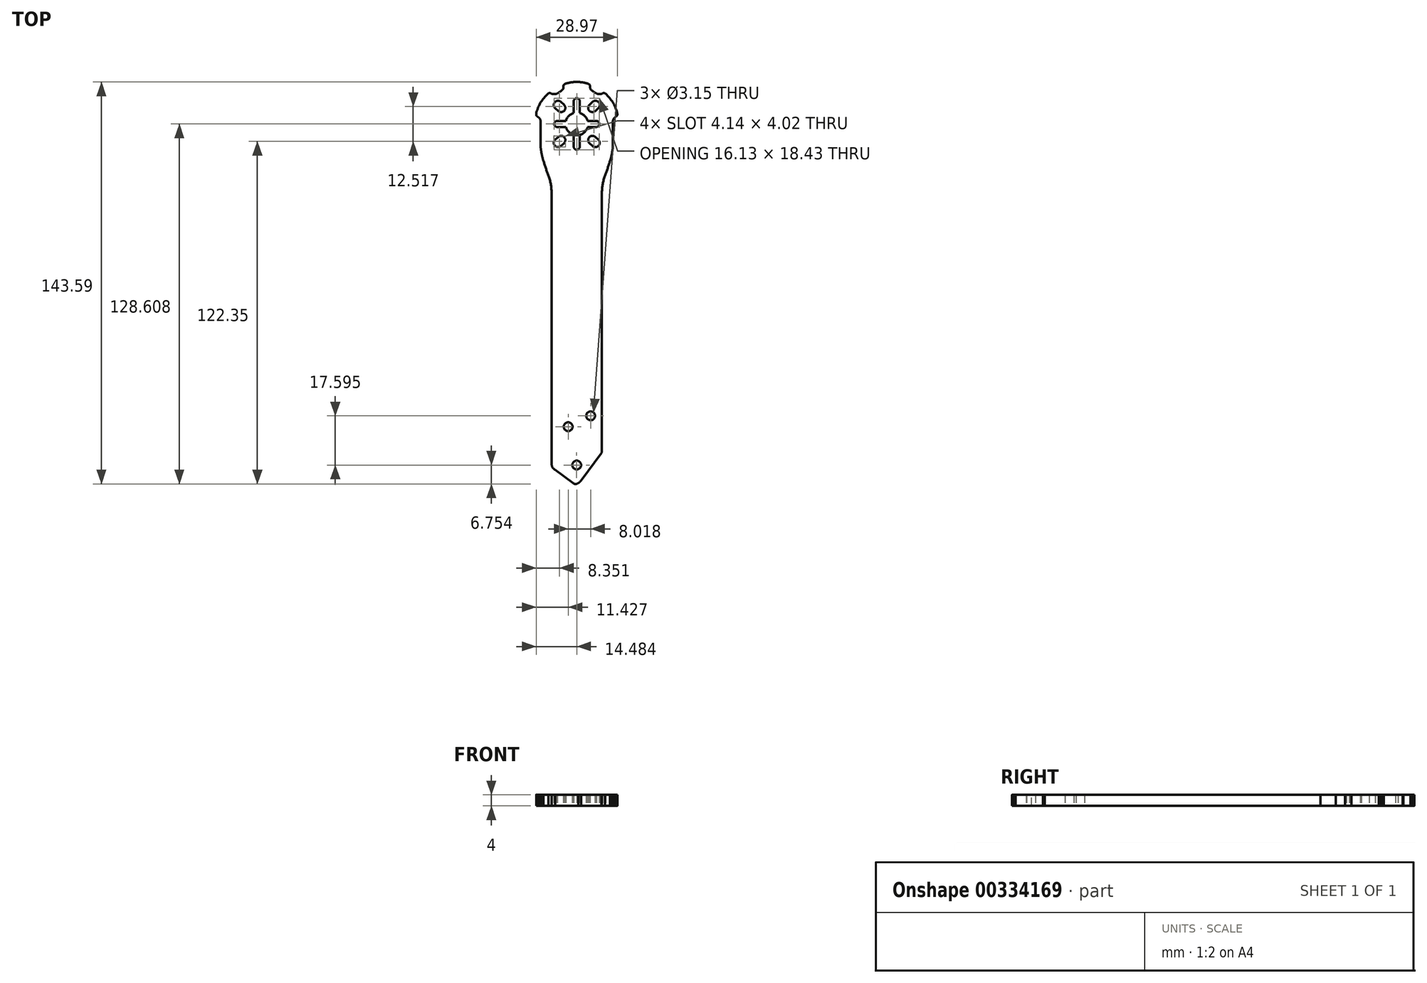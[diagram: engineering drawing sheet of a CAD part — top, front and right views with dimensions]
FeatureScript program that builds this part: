
annotation { "Feature Type Name" : "Feature", "Feature Type Description" : "" }
export const myFeature = defineFeature(function(context is Context, id is Id, definition is map)
    precondition{}
    {
        {
            var Q0;
            Q0=qCreatedBy(makeId("Top.planeOp"),FACE);
            var sketch = newSketch(context, id + "F0", { "sketchPlane" : qUnion([Q0])});
            skCircle(sketch, "E0", {"center": v(-4.22, -64.34) * mm, "radius": 1.57 * mm});
            skCircle(sketch, "E1", {"center": v(-12.24, -68.23) * mm, "radius": 1.57 * mm});
            skCircle(sketch, "E2", {"center": v(-9.2, -81.94) * mm, "radius": 1.57 * mm});
            skArc(sketch, "E3", {"start": v(-5.3, 41) * mm, "mid": v(-6.34, 42.79) * mm, "end": v(-8.13, 43.83) * mm});
            skArc(sketch, "E4", {"start": v(-1.12, 39.92) * mm, "mid": v(-1.4, 40.66) * mm, "end": v(-2.13, 41) * mm});
            skArc(sketch, "E5", {"start": v(-8.13, 48.05) * mm, "mid": v(-8.45, 48.82) * mm, "end": v(-9.22, 49.13) * mm});
            skLineSegment(sketch, "E6", {"start": v(-2.13, 41) * mm, "end": v(-5.3, 41) * mm});
            skLineSegment(sketch, "E7", {"start": v(-8.13, 48.05) * mm, "end": v(-8.13, 43.83) * mm});
            skLineSegment(sketch, "E8", {"start": v(-2.16, 45.18) * mm, "end": v(-2.16, 45.18) * mm});
            skArc(sketch, "E9", {"start": v(-4.61, 46.83) * mm, "mid": v(-4.74, 44.68) * mm, "end": v(-2.58, 44.55) * mm});
            skLineSegment(sketch, "E10", {"start": v(-3.52, 47.8) * mm, "end": v(-4.61, 46.83) * mm});
            skLineSegment(sketch, "E11", {"start": v(-2.58, 44.55) * mm, "end": v(-1.5, 45.52) * mm});
            skArc(sketch, "E12.trimOffspring", {"start": v(-1.5, 45.52) * mm, "mid": v(-1.37, 47.68) * mm, "end": v(-3.52, 47.8) * mm});
            skArc(sketch, "E13.MirrorCS", {"start": v(-1.5, 34.31) * mm, "mid": v(-1.37, 32.16) * mm, "end": v(-3.52, 32.03) * mm});
            skLineSegment(sketch, "E14.MirrorCS", {"start": v(-3.52, 32.03) * mm, "end": v(-4.61, 33) * mm});
            skArc(sketch, "E15.MirrorCS", {"start": v(-4.61, 33) * mm, "mid": v(-4.74, 35.16) * mm, "end": v(-2.58, 35.29) * mm});
            skLineSegment(sketch, "E16.MirrorCS", {"start": v(-2.58, 35.29) * mm, "end": v(-1.5, 34.31) * mm});
            skArc(sketch, "E17.MirrorCS", {"start": v(-1.12, 39.92) * mm, "mid": v(-1.4, 39.18) * mm, "end": v(-2.13, 38.84) * mm});
            skLineSegment(sketch, "E18.MirrorCS", {"start": v(-8.13, 31.79) * mm, "end": v(-8.13, 36) * mm});
            skLineSegment(sketch, "E19.MirrorCS", {"start": v(-2.13, 38.84) * mm, "end": v(-5.3, 38.84) * mm});
            skArc(sketch, "E20.MirrorCS", {"start": v(-5.3, 38.84) * mm, "mid": v(-6.34, 37.05) * mm, "end": v(-8.13, 36) * mm});
            skArc(sketch, "E21.MirrorCS", {"start": v(-8.13, 31.79) * mm, "mid": v(-8.45, 31.02) * mm, "end": v(-9.22, 30.7) * mm});
            skArc(sketch, "E22", {"start": v(0.93, 21.46) * mm, "mid": v(0.09, 18.5) * mm, "end": v(-0.19, 15.46) * mm});
            skArc(sketch, "E23", {"start": v(0.93, 21.46) * mm, "mid": v(1.86, 24.11) * mm, "end": v(2.71, 26.8) * mm});
            skArc(sketch, "E24", {"start": v(2.71, 26.8) * mm, "mid": v(3.17, 28.42) * mm, "end": v(3.5, 30.09) * mm});
            skArc(sketch, "E25", {"start": v(3.5, 30.09) * mm, "mid": v(3.66, 31.29) * mm, "end": v(3.74, 32.5) * mm});
            skLineSegment(sketch, "E26", {"start": v(3.74, 32.5) * mm, "end": v(3.74, 40.9) * mm});
            skArc(sketch, "E27", {"start": v(4.33, 42.17) * mm, "mid": v(3.9, 41.6) * mm, "end": v(3.74, 40.9) * mm});
            skArc(sketch, "E28", {"start": v(4.95, 42.62) * mm, "mid": v(4.64, 42.4) * mm, "end": v(4.33, 42.17) * mm});
            skArc(sketch, "E29", {"start": v(4.95, 42.62) * mm, "mid": v(5.2, 42.9) * mm, "end": v(5.3, 43.27) * mm});
            skArc(sketch, "E30", {"start": v(5.3, 43.27) * mm, "mid": v(5.28, 43.63) * mm, "end": v(5.2, 43.98) * mm});
            skArc(sketch, "E31", {"start": v(5.2, 43.98) * mm, "mid": v(3.66, 47.64) * mm, "end": v(1.1, 50.68) * mm});
            skArc(sketch, "E32", {"start": v(1.1, 50.68) * mm, "mid": v(0.6, 50.95) * mm, "end": v(0.04, 50.85) * mm});
            skArc(sketch, "E33", {"start": v(-2.22, 50.85) * mm, "mid": v(-1.09, 50.55) * mm, "end": v(0.04, 50.85) * mm});
            skArc(sketch, "E34", {"start": v(-4.01, 52.04) * mm, "mid": v(-3.15, 51.4) * mm, "end": v(-2.22, 50.85) * mm});
            skArc(sketch, "E35", {"start": v(-4.39, 52.76) * mm, "mid": v(-4.27, 52.36) * mm, "end": v(-4.01, 52.04) * mm});
            skArc(sketch, "E36", {"start": v(-4.45, 53.55) * mm, "mid": v(-4.42, 53.15) * mm, "end": v(-4.39, 52.76) * mm});
            skArc(sketch, "E37", {"start": v(-4.45, 53.55) * mm, "mid": v(-4.62, 53.95) * mm, "end": v(-4.96, 54.22) * mm});
            skArc(sketch, "E38", {"start": v(-4.96, 54.22) * mm, "mid": v(-7.06, 54.75) * mm, "end": v(-9.22, 54.9) * mm});
            skArc(sketch, "E39", {"start": v(-18.19, -81.72) * mm, "mid": v(-17.77, -82.83) * mm, "end": v(-16.92, -83.66) * mm});
            skLineSegment(sketch, "E40", {"start": v(-16.92, -83.66) * mm, "end": v(-10.54, -88.38) * mm});
            skArc(sketch, "E41", {"start": v(-10.54, -88.38) * mm, "mid": v(-9.6, -88.7) * mm, "end": v(-8.66, -88.38) * mm});
            skArc(sketch, "E42", {"start": v(-8.66, -88.38) * mm, "mid": v(-8.1, -87.97) * mm, "end": v(-7.64, -87.45) * mm});
            skLineSegment(sketch, "E43", {"start": v(-7.64, -87.45) * mm, "end": v(-0.42, -77.68) * mm});
            skArc(sketch, "E44", {"start": v(-0.42, -77.68) * mm, "mid": v(-0.26, -77.4) * mm, "end": v(-0.19, -77.07) * mm});
            skPoint(sketch, "E45", {"position": v(-9.19, 15.46) * mm});
            skLineSegment(sketch, "E46", {"start": v(-9.19, 54.9) * mm, "end": v(-9.19, -88.64) * mm});
            skArc(sketch, "E47.MirrorCS", {"start": v(-13.4, 54.22) * mm, "mid": v(-11.31, 54.75) * mm, "end": v(-9.15, 54.9) * mm});
            skArc(sketch, "E48.MirrorCS", {"start": v(-13.92, 53.55) * mm, "mid": v(-13.75, 53.95) * mm, "end": v(-13.4, 54.22) * mm});
            skArc(sketch, "E49.MirrorCS", {"start": v(-13.92, 53.55) * mm, "mid": v(-13.95, 53.15) * mm, "end": v(-13.98, 52.76) * mm});
            skArc(sketch, "E50.MirrorCS", {"start": v(-13.98, 52.76) * mm, "mid": v(-14.1, 52.36) * mm, "end": v(-14.36, 52.04) * mm});
            skArc(sketch, "E51.MirrorCS", {"start": v(-14.36, 52.04) * mm, "mid": v(-15.22, 51.4) * mm, "end": v(-16.16, 50.85) * mm});
            skArc(sketch, "E52.MirrorCS", {"start": v(-16.16, 50.85) * mm, "mid": v(-17.29, 50.55) * mm, "end": v(-18.42, 50.85) * mm});
            skArc(sketch, "E53.MirrorCS", {"start": v(-19.48, 50.68) * mm, "mid": v(-18.98, 50.95) * mm, "end": v(-18.42, 50.85) * mm});
            skArc(sketch, "E54.MirrorCS", {"start": v(-23.57, 43.98) * mm, "mid": v(-22.03, 47.64) * mm, "end": v(-19.48, 50.68) * mm});
            skArc(sketch, "E55.MirrorCS", {"start": v(-16.88, 45.52) * mm, "mid": v(-17, 47.68) * mm, "end": v(-14.85, 47.8) * mm});
            skLineSegment(sketch, "E56.MirrorCS", {"start": v(-14.85, 47.8) * mm, "end": v(-13.76, 46.83) * mm});
            skArc(sketch, "E57.MirrorCS", {"start": v(-13.76, 46.83) * mm, "mid": v(-13.63, 44.68) * mm, "end": v(-15.79, 44.55) * mm});
            skLineSegment(sketch, "E58.MirrorCS", {"start": v(-15.79, 44.55) * mm, "end": v(-16.88, 45.52) * mm});
            skArc(sketch, "E59.MirrorCS", {"start": v(-10.24, 48.05) * mm, "mid": v(-9.92, 48.82) * mm, "end": v(-9.15, 49.13) * mm});
            skLineSegment(sketch, "E60.MirrorCS", {"start": v(-10.24, 48.05) * mm, "end": v(-10.24, 43.83) * mm});
            skArc(sketch, "E61.MirrorCS", {"start": v(-23.67, 43.27) * mm, "mid": v(-23.65, 43.63) * mm, "end": v(-23.57, 43.98) * mm});
            skArc(sketch, "E62.MirrorCS", {"start": v(-23.32, 42.62) * mm, "mid": v(-23.57, 42.9) * mm, "end": v(-23.67, 43.27) * mm});
            skArc(sketch, "E63.MirrorCS", {"start": v(-23.32, 42.62) * mm, "mid": v(-23, 42.4) * mm, "end": v(-22.7, 42.17) * mm});
            skArc(sketch, "E64.MirrorCS", {"start": v(-22.7, 42.17) * mm, "mid": v(-22.27, 41.6) * mm, "end": v(-22.11, 40.9) * mm});
            skLineSegment(sketch, "E65.MirrorCS", {"start": v(-22.11, 32.5) * mm, "end": v(-22.11, 40.9) * mm});
            skArc(sketch, "E66.MirrorCS", {"start": v(-13.07, 41) * mm, "mid": v(-12.03, 42.79) * mm, "end": v(-10.24, 43.83) * mm});
            skLineSegment(sketch, "E67.MirrorCS", {"start": v(-16.25, 41) * mm, "end": v(-13.07, 41) * mm});
            skArc(sketch, "E68.MirrorCS", {"start": v(-17.25, 39.92) * mm, "mid": v(-16.96, 40.66) * mm, "end": v(-16.25, 41) * mm});
            skArc(sketch, "E69.MirrorCS", {"start": v(-17.25, 39.92) * mm, "mid": v(-16.96, 39.18) * mm, "end": v(-16.25, 38.84) * mm});
            skLineSegment(sketch, "E70.MirrorCS", {"start": v(-16.25, 38.84) * mm, "end": v(-13.07, 38.84) * mm});
            skArc(sketch, "E71.MirrorCS", {"start": v(-13.07, 38.84) * mm, "mid": v(-12.03, 37.05) * mm, "end": v(-10.24, 36) * mm});
            skLineSegment(sketch, "E72.MirrorCS", {"start": v(-10.24, 31.79) * mm, "end": v(-10.24, 36) * mm});
            skArc(sketch, "E73.MirrorCS", {"start": v(-10.24, 31.79) * mm, "mid": v(-9.92, 31.02) * mm, "end": v(-9.15, 30.7) * mm});
            skArc(sketch, "E74.MirrorCS", {"start": v(-13.76, 33) * mm, "mid": v(-13.63, 35.16) * mm, "end": v(-15.79, 35.29) * mm});
            skLineSegment(sketch, "E75.MirrorCS", {"start": v(-15.79, 35.29) * mm, "end": v(-16.88, 34.31) * mm});
            skArc(sketch, "E76.MirrorCS", {"start": v(-16.88, 34.31) * mm, "mid": v(-17, 32.16) * mm, "end": v(-14.85, 32.03) * mm});
            skLineSegment(sketch, "E77.MirrorCS", {"start": v(-14.85, 32.03) * mm, "end": v(-13.76, 33) * mm});
            skArc(sketch, "E78.MirrorCS", {"start": v(-21.87, 30.09) * mm, "mid": v(-22.04, 31.29) * mm, "end": v(-22.11, 32.5) * mm});
            skArc(sketch, "E79.MirrorCS", {"start": v(-21.08, 26.8) * mm, "mid": v(-21.55, 28.42) * mm, "end": v(-21.87, 30.09) * mm});
            skArc(sketch, "E80.MirrorCS", {"start": v(-19.3, 21.46) * mm, "mid": v(-20.23, 24.11) * mm, "end": v(-21.08, 26.8) * mm});
            skArc(sketch, "E81.MirrorCS", {"start": v(-19.3, 21.46) * mm, "mid": v(-18.46, 18.5) * mm, "end": v(-18.19, 15.46) * mm});
            skLineSegment(sketch, "E82", {"start": v(-12.24, -68.23) * mm, "end": v(-9.19, -68.23) * mm});
            skLineSegment(sketch, "E83", {"start": v(-4.22, -64.34) * mm, "end": v(-9.19, -64.34) * mm});
            skLineSegment(sketch, "E84.trimOffspring", {"start": v(-18.19, 15.46) * mm, "end": v(-18.19, 15.46) * mm});
            skLineSegment(sketch, "E85", {"start": v(-18.19, 15.46) * mm, "end": v(-18.19, -81.73) * mm});
            skLineSegment(sketch, "E86", {"start": v(-0.19, 15.46) * mm, "end": v(-0.19, -77.07) * mm});
            skLineSegment(sketch, "E87", {"start": v(-0.19, -55.55) * mm, "end": v(-18.19, -55.55) * mm});
            skLineSegment(sketch, "E88", {"start": v(-0.19, 3.48) * mm, "end": v(-18.19, 3.48) * mm});
            skLineSegment(sketch, "E89", {"start": v(-0.19, 13.23) * mm, "end": v(-18.19, 13.23) * mm});
            skSolve(sketch);
        }
        {
            var Q0;
            Q0=qSketchRegion(id+"F0",true);
            extrude(context, id + "F1", {"entities" : qUnion([Q0]), "depth" : 4 * mm});
        }
    });
